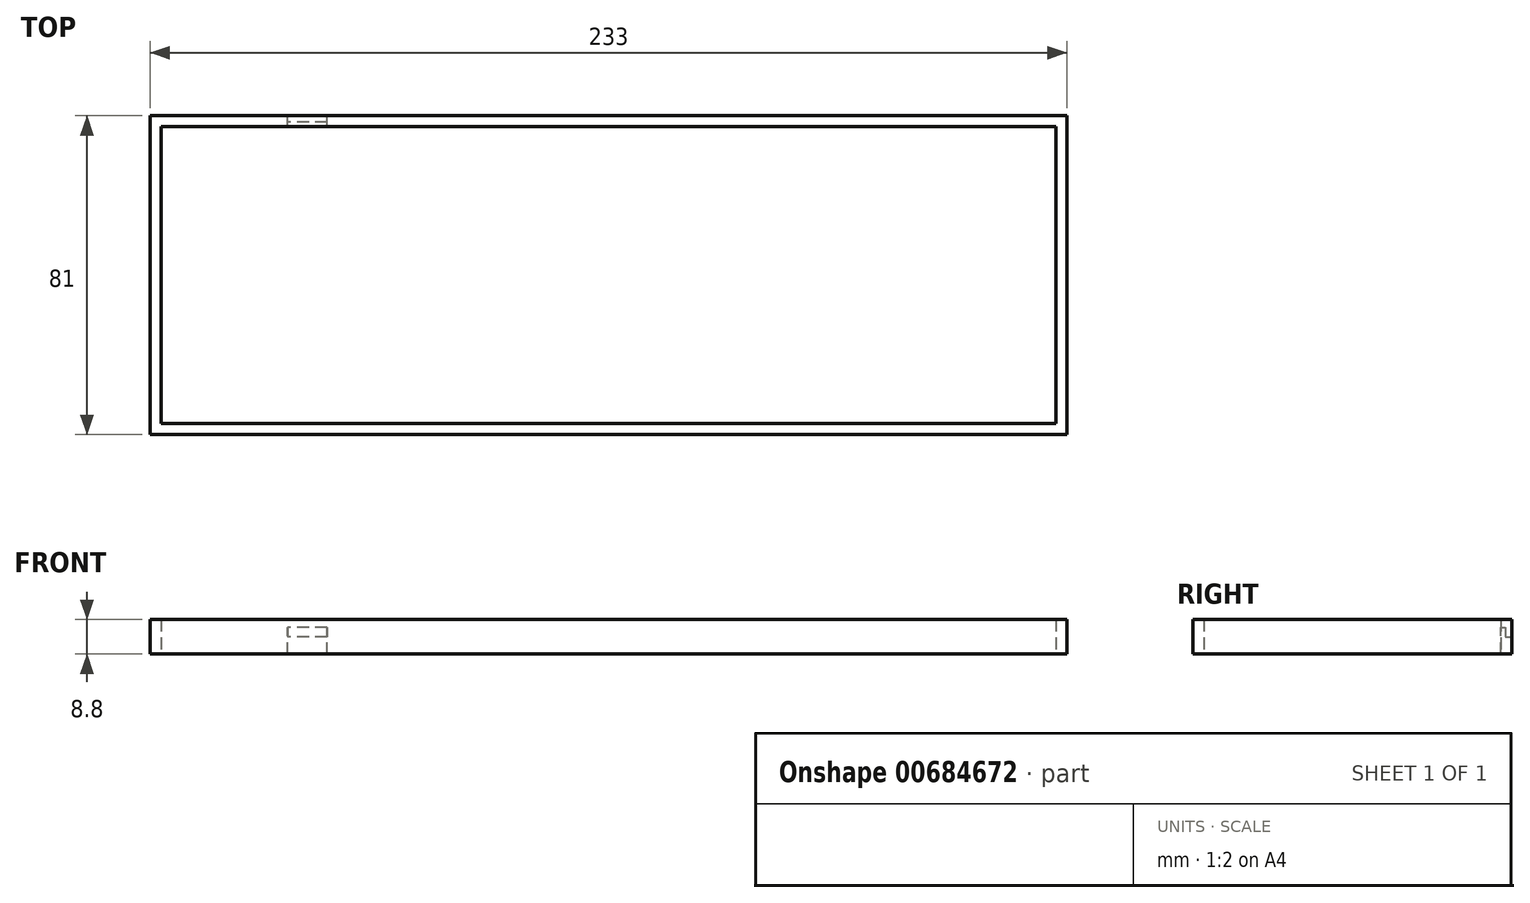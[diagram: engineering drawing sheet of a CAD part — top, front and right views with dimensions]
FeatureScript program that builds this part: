
annotation { "Feature Type Name" : "Feature", "Feature Type Description" : "" }
export const myFeature = defineFeature(function(context is Context, id is Id, definition is map)
    precondition{}
    {
        {
            var Q0;
            Q0=qCreatedBy(makeId("Top.planeOp"),FACE);
            var sketch = newSketch(context, id + "F0", { "sketchPlane" : qUnion([Q0])});
            skLineSegment(sketch, "E0.bottom", {"start": v(116.5, 40.5) * mm, "end": v(-116.5, 40.5) * mm});
            skLineSegment(sketch, "E0.top", {"start": v(116.5, -40.5) * mm, "end": v(-116.5, -40.5) * mm});
            skLineSegment(sketch, "E0.left", {"start": v(116.5, 40.5) * mm, "end": v(116.5, -40.5) * mm});
            skLineSegment(sketch, "E0.right", {"start": v(-116.5, 40.5) * mm, "end": v(-116.5, -40.5) * mm});
            skPoint(sketch, "E0.middle", {"position": v(0, 0) * mm});
            skLineSegment(sketch, "E1.bottom", {"start": v(-113.7, 37.7) * mm, "end": v(113.7, 37.7) * mm});
            skLineSegment(sketch, "E1.top", {"start": v(-113.7, -37.7) * mm, "end": v(113.7, -37.7) * mm});
            skLineSegment(sketch, "E1.left", {"start": v(-113.7, 37.7) * mm, "end": v(-113.7, -37.7) * mm});
            skLineSegment(sketch, "E1.right", {"start": v(113.7, 37.7) * mm, "end": v(113.7, -37.7) * mm});
            skSolve(sketch);
        }
        {
            var Q0;
            Q0=makeQuery(id+"F0.imprint","IMPRINT",FACE,{"disambiguationData":[TD([[makeQuery(id+"F0.imprint","IMPRINT",EDGE,{"derivedFrom":sQuery(id+"F0.wireOp",EDGE,"E0.bottom")}),1.0]])]});
            extrude(context, id + "F1", {"entities" : qUnion([Q0]), "depth" : 8.8 * mm, "offsetDistance" : 25 * mm});
        }
        {
            var Q0;
            Q0=makeQuery(id+"F1.opExtrude","SWEPT_FACE",FACE,{"disambiguationData":[OSD([sQuery(id+"F0.wireOp",EDGE,"E0.bottom")])]});
            var sketch = newSketch(context, id + "F2", { "sketchPlane" : qUnion([Q0])});
            skLineSegment(sketch, "E2.bottom", {"start": v(71.5, 0) * mm, "end": v(81.5, 0) * mm});
            skLineSegment(sketch, "E2.top", {"start": v(71.5, 4.4) * mm, "end": v(81.5, 4.4) * mm});
            skLineSegment(sketch, "E2.left", {"start": v(71.5, 0) * mm, "end": v(71.5, 4.4) * mm});
            skLineSegment(sketch, "E2.right", {"start": v(81.5, 0) * mm, "end": v(81.5, 4.4) * mm});
            skPoint(sketch, "E2.middle", {"position": v(76.5, 2.2) * mm});
            skSolve(sketch);
        }
        {
            var Q0;
            Q0=makeQuery(id+"F2.imprint","IMPRINT",FACE,{"disambiguationData":[TD([[makeQuery(id+"F2.imprint","IMPRINT",EDGE,{"derivedFrom":sQuery(id+"F2.wireOp",EDGE,"E2.bottom")}),1.0]])]});
            extrude(context, id + "F3", {"entities" : qUnion([Q0]), "operationType" : NewBodyOperationType.REMOVE, "oppositeDirection" : true, "depth" : 25 * mm, "offsetDistance" : 25 * mm});
        }
        {
            var Q0;
            Q0=makeQuery(id+"F3.boolean.opBoolean","COPY",FACE,{"derivedFrom":makeQuery(id+"F3.opExtrude","SWEPT_FACE",FACE,{"disambiguationData":[OSD([sQuery(id+"F2.wireOp",EDGE,"E2.top")])]})});
            var sketch = newSketch(context, id + "F4", { "sketchPlane" : qUnion([Q0])});
            skLineSegment(sketch, "E3.bottom", {"start": v(-71.5, -37.7) * mm, "end": v(-81.5, -37.7) * mm});
            skLineSegment(sketch, "E3.top", {"start": v(-71.5, -38.9) * mm, "end": v(-81.5, -38.9) * mm});
            skLineSegment(sketch, "E3.left", {"start": v(-71.5, -37.7) * mm, "end": v(-71.5, -38.9) * mm});
            skLineSegment(sketch, "E3.right", {"start": v(-81.5, -37.7) * mm, "end": v(-81.5, -38.9) * mm});
            skSolve(sketch);
        }
        {
            var Q0;
            Q0=makeQuery(id+"F4.imprint","IMPRINT",FACE,{"disambiguationData":[TD([[makeQuery(id+"F4.imprint","IMPRINT",EDGE,{"derivedFrom":sQuery(id+"F4.wireOp",EDGE,"E3.bottom")}),1.0]])]});
            extrude(context, id + "F5", {"entities" : qUnion([Q0]), "operationType" : NewBodyOperationType.REMOVE, "oppositeDirection" : true, "depth" : 2.4 * mm, "offsetDistance" : 25 * mm});
        }
    });
